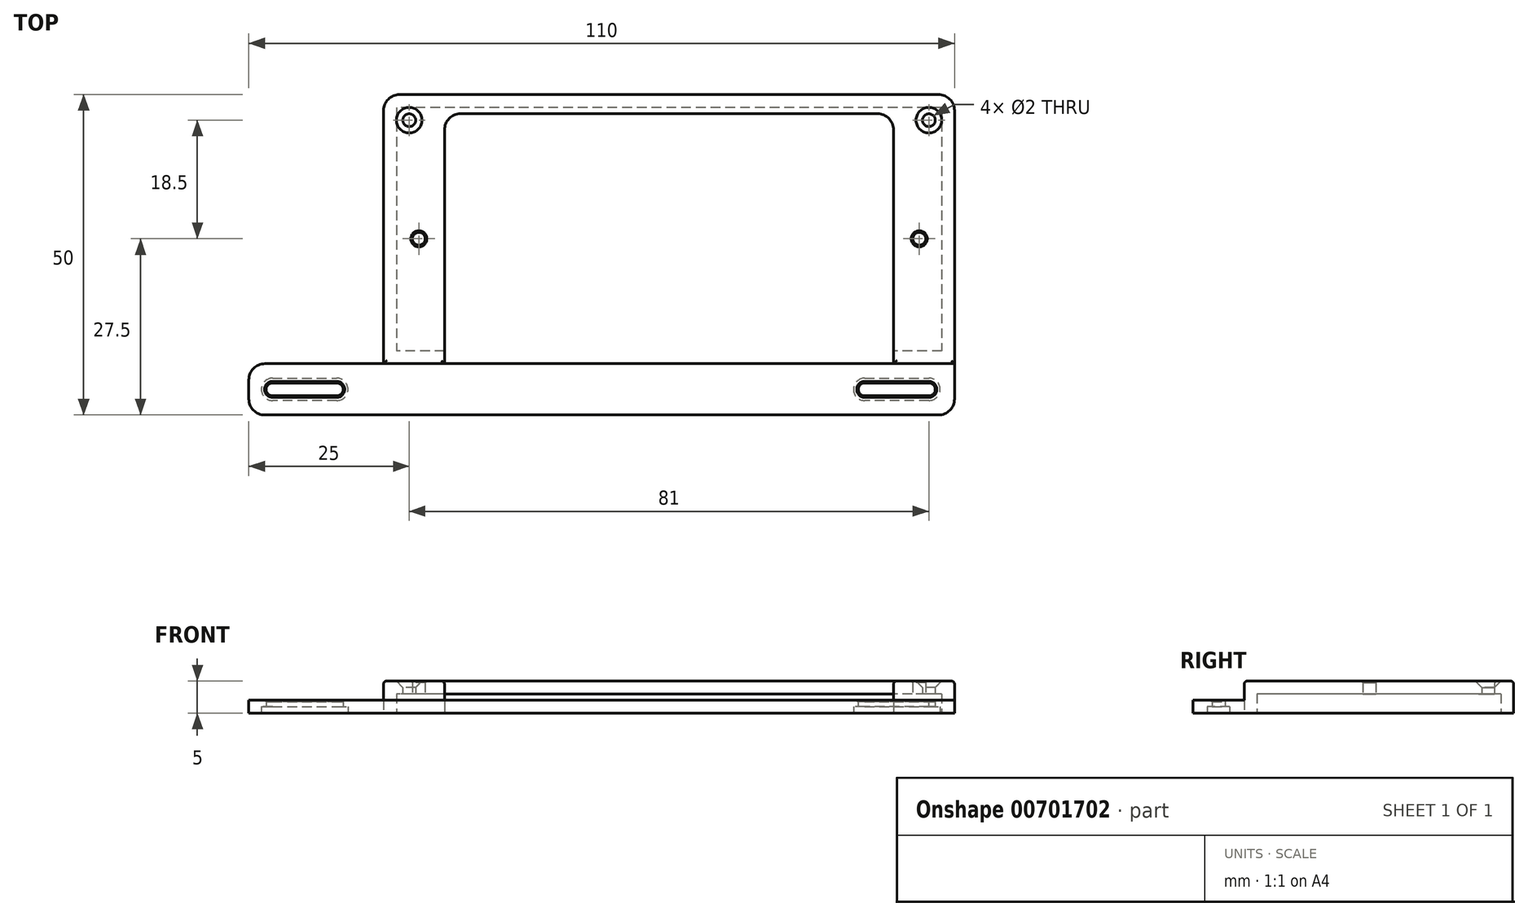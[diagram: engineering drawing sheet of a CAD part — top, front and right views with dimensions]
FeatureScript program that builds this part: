
annotation { "Feature Type Name" : "Feature", "Feature Type Description" : "" }
export const myFeature = defineFeature(function(context is Context, id is Id, definition is map)
    precondition{}
    {
        {
            var Q0;
            Q0=qCreatedBy(makeId("Top.planeOp"),FACE);
            var sketch = newSketch(context, id + "F0", { "sketchPlane" : qUnion([Q0])});
            skLineSegment(sketch, "E0.bottom", {"start": v(44.5, -22.5) * mm, "end": v(-44.5, -22.5) * mm});
            skLineSegment(sketch, "E0.top", {"start": v(44.5, 22.5) * mm, "end": v(-44.5, 22.5) * mm});
            skLineSegment(sketch, "E0.left", {"start": v(44.5, -22.5) * mm, "end": v(44.5, 22.5) * mm});
            skLineSegment(sketch, "E0.right", {"start": v(-44.5, -22.5) * mm, "end": v(-44.5, 22.5) * mm});
            skPoint(sketch, "E0.middle", {"position": v(0, 0) * mm});
            skSolve(sketch);
        }
        {
            var Q0;
            Q0=qCreatedBy(makeId("Top.planeOp"),FACE);
            var sketch = newSketch(context, id + "F1", { "sketchPlane" : qUnion([Q0])});
            skLineSegment(sketch, "E1.bottom", {"start": v(35, -19.5) * mm, "end": v(-35, -19.5) * mm});
            skLineSegment(sketch, "E1.top", {"start": v(35, 19.5) * mm, "end": v(-35, 19.5) * mm});
            skLineSegment(sketch, "E1.left", {"start": v(35, -19.5) * mm, "end": v(35, 19.5) * mm});
            skLineSegment(sketch, "E1.right", {"start": v(-35, -19.5) * mm, "end": v(-35, 19.5) * mm});
            skPoint(sketch, "E1.middle", {"position": v(0, 0) * mm});
            skSolve(sketch);
        }
        {
            var Q0;
            Q0=qCreatedBy(makeId("Top.planeOp"),FACE);
            var sketch = newSketch(context, id + "F2", { "sketchPlane" : qUnion([Q0])});
            skLineSegment(sketch, "E2.bottom", {"start": v(44.5, -19.5) * mm, "end": v(-65.5, -19.5) * mm});
            skLineSegment(sketch, "E2.top", {"start": v(44.5, -27.5) * mm, "end": v(-65.5, -27.5) * mm});
            skLineSegment(sketch, "E2.left", {"start": v(44.5, -19.5) * mm, "end": v(44.5, -27.5) * mm});
            skLineSegment(sketch, "E2.right", {"start": v(-65.5, -19.5) * mm, "end": v(-65.5, -27.5) * mm});
            skSolve(sketch);
        }
        {
            var Q0;
            Q0 = qSketchRegion(id + "F0", true);
            var Q1;
            Q1 = qSketchRegion(id + "F2", true);
            extrude(context, id + "F3", {"entities" : qUnion([Q0, Q1]), "depth" : 2 * mm, "offsetDistance" : 25 * mm});
        }
        {
            var Q0;
            Q0=qCreatedBy(makeId("Top.planeOp"),FACE);
            var sketch = newSketch(context, id + "F4", { "sketchPlane" : qUnion([Q0])});
            skLineSegment(sketch, "E3.bottom", {"start": v(-44.5, 22.5) * mm, "end": v(44.5, 22.5) * mm});
            skLineSegment(sketch, "E3.top", {"start": v(-44.5, -19.5) * mm, "end": v(44.5, -19.5) * mm});
            skLineSegment(sketch, "E3.left", {"start": v(-44.5, 22.5) * mm, "end": v(-44.5, -19.5) * mm});
            skLineSegment(sketch, "E3.right", {"start": v(44.5, 22.5) * mm, "end": v(44.5, -19.5) * mm});
            skSolve(sketch);
        }
        {
            var Q0;
            Q0 = qSketchRegion(id + "F4", true);
            extrude(context, id + "F5", {"entities" : qUnion([Q0]), "depth" : 5 * mm, "offsetDistance" : 25 * mm});
        }
        {
            var Q0;
            Q0=qCreatedBy(makeId("Top.planeOp"),FACE);
            var sketch = newSketch(context, id + "F6", { "sketchPlane" : qUnion([Q0])});
            skLineSegment(sketch, "E4.bottom", {"start": v(42.5, 20.5) * mm, "end": v(-42.5, 20.5) * mm});
            skLineSegment(sketch, "E4.top", {"start": v(42.5, -17.5) * mm, "end": v(-42.5, -17.5) * mm});
            skLineSegment(sketch, "E4.left", {"start": v(42.5, 20.5) * mm, "end": v(42.5, -17.5) * mm});
            skLineSegment(sketch, "E4.right", {"start": v(-42.5, 20.5) * mm, "end": v(-42.5, -17.5) * mm});
            skSolve(sketch);
        }
        {
            var Q0;
            Q0 = qSketchRegion(id + "F6", true);
            extrude(context, id + "F7", {"entities" : qUnion([Q0]), "operationType" : NewBodyOperationType.REMOVE, "depth" : 3 * mm, "offsetDistance" : 25 * mm});
        }
        {
            var Q0;
            Q0 = qSketchRegion(id + "F1", true);
            extrude(context, id + "F8", {"entities" : qUnion([Q0]), "operationType" : NewBodyOperationType.REMOVE, "depth" : 25 * mm, "offsetDistance" : 25 * mm});
        }
        {
            var Q0;
            Q0=makeQuery(id+"F3.opExtrude","SWEPT_BODY",BODY,{"disambiguationData":[OSD([sQuery(id+"F0.wireOp",EDGE,"E0.bottom"),sQuery(id+"F0.wireOp",EDGE,"E0.top"),sQuery(id+"F0.wireOp",EDGE,"E0.left"),sQuery(id+"F0.wireOp",EDGE,"E0.right")])]});
            var Q1;
            Q1=makeQuery(id+"F5.opExtrude","SWEPT_BODY",BODY,{"disambiguationData":[OSD([sQuery(id+"F4.wireOp",EDGE,"E3.bottom"),sQuery(id+"F4.wireOp",EDGE,"E3.top"),sQuery(id+"F4.wireOp",EDGE,"E3.left"),sQuery(id+"F4.wireOp",EDGE,"E3.right")])]});
            var Q2;
            Q2=makeQuery(id+"F3.opExtrude","SWEPT_BODY",BODY,{"disambiguationData":[OSD([sQuery(id+"F2.wireOp",EDGE,"E2.bottom"),sQuery(id+"F2.wireOp",EDGE,"E2.top"),sQuery(id+"F2.wireOp",EDGE,"E2.left"),sQuery(id+"F2.wireOp",EDGE,"E2.right")])]});
            booleanBodies(context, id + "F9", {"operationType" : BooleanOperationType.UNION, "tools" : qUnion([Q0, Q1, Q2])});
        }
        {
            var Q0;
            Q0=qCreatedBy(makeId("Top.planeOp"),FACE);
            var sketch = newSketch(context, id + "F10", { "sketchPlane" : qUnion([Q0])});
            skCircle(sketch, "E5", {"center": v(-40.5, 18.5) * mm, "radius": 1 * mm});
            skCircle(sketch, "E6", {"center": v(40.5, 18.5) * mm, "radius": 1 * mm});
            skSolve(sketch);
        }
        {
            var Q0;
            Q0=makeQuery(id+"F10.imprint","IMPRINT",FACE,{"disambiguationData":[TD([[makeQuery(id+"F10.imprint","IMPRINT",EDGE,{"derivedFrom":sQuery(id+"F10.wireOp",EDGE,"E5")}),1.0]])]});
            var Q1;
            Q1=makeQuery(id+"F10.imprint","IMPRINT",FACE,{"disambiguationData":[TD([[makeQuery(id+"F10.imprint","IMPRINT",EDGE,{"derivedFrom":sQuery(id+"F10.wireOp",EDGE,"E6")}),1.0]])]});
            extrude(context, id + "F11", {"entities" : qUnion([Q0, Q1]), "operationType" : NewBodyOperationType.REMOVE, "depth" : 25 * mm, "offsetDistance" : 25 * mm});
        }
        {
            var Q0;
            Q0=qCreatedBy(makeId("Top.planeOp"),FACE);
            var sketch = newSketch(context, id + "F12", { "sketchPlane" : qUnion([Q0])});
            skCircle(sketch, "E7", {"center": v(-39, 0) * mm, "radius": 1 * mm});
            skCircle(sketch, "E8", {"center": v(39, 0) * mm, "radius": 1 * mm});
            skSolve(sketch);
        }
        {
            var Q0;
            Q0 = qSketchRegion(id + "F12", true);
            extrude(context, id + "F13", {"entities" : qUnion([Q0]), "operationType" : NewBodyOperationType.REMOVE, "depth" : 25 * mm, "offsetDistance" : 25 * mm});
        }
        {
            var Q0;
            Q0=makeQuery(id+"F11.boolean.opBoolean","INTERSECT",EDGE,{"derivedFrom":[makeQuery(id+"F5.opExtrude","CAP_FACE",FACE,{"disambiguationData":[OSD([sQuery(id+"F4.wireOp",EDGE,"E3.bottom"),sQuery(id+"F4.wireOp",EDGE,"E3.top"),sQuery(id+"F4.wireOp",EDGE,"E3.left"),sQuery(id+"F4.wireOp",EDGE,"E3.right")])],"isStart":false}),makeQuery(id+"F11.opExtrude","SWEPT_FACE",FACE,{"disambiguationData":[OSD([sQuery(id+"F10.wireOp",EDGE,"E5")])]})]});
            var Q1;
            Q1=makeQuery(id+"F11.boolean.opBoolean","INTERSECT",EDGE,{"derivedFrom":[makeQuery(id+"F5.opExtrude","CAP_FACE",FACE,{"disambiguationData":[OSD([sQuery(id+"F4.wireOp",EDGE,"E3.bottom"),sQuery(id+"F4.wireOp",EDGE,"E3.top"),sQuery(id+"F4.wireOp",EDGE,"E3.left"),sQuery(id+"F4.wireOp",EDGE,"E3.right")])],"isStart":false}),makeQuery(id+"F11.opExtrude","SWEPT_FACE",FACE,{"disambiguationData":[OSD([sQuery(id+"F10.wireOp",EDGE,"E6")])]})]});
            chamfer(context, id + "F14", {"entities" : qUnion([Q0, Q1]), "chamferType" : ChamferType.OFFSET_ANGLE, "width" : 1 * mm, "oppositeDirection" : false, "angle" : 45 * degree, "tangentPropagation" : true});
        }
        {
            var Q0;
            Q0=makeQuery(id+"F9.opBoolean","MERGE",EDGE,{"derivedFrom":[makeQuery(id+"F3.opExtrude","SWEPT_EDGE",EDGE,{"disambiguationData":[OSD([sQuery(id+"F0.wireOp",EDGE,"E0.top"),sQuery(id+"F0.wireOp",EDGE,"E0.right")])]}),makeQuery(id+"F5.opExtrude","SWEPT_EDGE",EDGE,{"disambiguationData":[OSD([sQuery(id+"F4.wireOp",EDGE,"E3.bottom"),sQuery(id+"F4.wireOp",EDGE,"E3.left")])]})]});
            var Q1;
            Q1=makeQuery(id+"F9.opBoolean","MERGE",EDGE,{"derivedFrom":[makeQuery(id+"F3.opExtrude","SWEPT_EDGE",EDGE,{"disambiguationData":[OSD([sQuery(id+"F0.wireOp",EDGE,"E0.top"),sQuery(id+"F0.wireOp",EDGE,"E0.left")])]}),makeQuery(id+"F5.opExtrude","SWEPT_EDGE",EDGE,{"disambiguationData":[OSD([sQuery(id+"F4.wireOp",EDGE,"E3.bottom"),sQuery(id+"F4.wireOp",EDGE,"E3.right")])]})]});
            var Q2;
            Q2=makeQuery(id+"F3.opExtrude","SWEPT_EDGE",EDGE,{"disambiguationData":[OSD([sQuery(id+"F2.wireOp",EDGE,"E2.top"),sQuery(id+"F2.wireOp",EDGE,"E2.left")])]});
            var Q3;
            Q3=makeQuery(id+"F3.opExtrude","SWEPT_EDGE",EDGE,{"disambiguationData":[OSD([sQuery(id+"F2.wireOp",EDGE,"E2.top"),sQuery(id+"F2.wireOp",EDGE,"E2.right")])]});
            var Q4;
            Q4=makeQuery(id+"F3.opExtrude","SWEPT_EDGE",EDGE,{"disambiguationData":[OSD([sQuery(id+"F2.wireOp",EDGE,"E2.bottom"),sQuery(id+"F2.wireOp",EDGE,"E2.right")])]});
            var Q5;
            Q5=makeQuery(id+"F8.boolean.opBoolean","COPY",EDGE,{"derivedFrom":makeQuery(id+"F8.opExtrude","SWEPT_EDGE",EDGE,{"disambiguationData":[OSD([sQuery(id+"F1.wireOp",EDGE,"E1.top"),sQuery(id+"F1.wireOp",EDGE,"E1.right")])]})});
            var Q6;
            Q6=makeQuery(id+"F8.boolean.opBoolean","COPY",EDGE,{"derivedFrom":makeQuery(id+"F8.opExtrude","SWEPT_EDGE",EDGE,{"disambiguationData":[OSD([sQuery(id+"F1.wireOp",EDGE,"E1.top"),sQuery(id+"F1.wireOp",EDGE,"E1.left")])]})});
            fillet(context, id + "F15", {"entities" : qUnion([Q0, Q1, Q2, Q3, Q4, Q5, Q6]), "radius" : 2.5 * mm, "tangentPropagation" : true, "allowEdgeOverflow" : false});
        }
        {
            var Q0;
            {var subQ0=sQuery(id+"F4.wireOp",EDGE,"E3.left");var subQ1=sQuery(id+"F4.wireOp",EDGE,"E3.top");Q0=makeQuery(id+"F8.boolean.opBoolean","SPLIT",EDGE,{"disambiguationData":[TD([makeQuery(id+"F5.opExtrude","SWEPT_FACE",FACE,{"disambiguationData":[OSD([subQ0])]})])],"derivedFrom":makeQuery(id+"F5.opExtrude","CAP_EDGE",EDGE,{"disambiguationData":[OSD([subQ1])],"isStart":false})});}
            var Q1;
            Q1=makeQuery(id+"F5.opExtrude","CAP_EDGE",EDGE,{"disambiguationData":[OSD([sQuery(id+"F4.wireOp",EDGE,"E3.left")])],"isStart":false});
            var Q2;
            Q2=makeQuery(id+"F8.boolean.opBoolean","INTERSECT",EDGE,{"derivedFrom":[makeQuery(id+"F5.opExtrude","CAP_FACE",FACE,{"disambiguationData":[OSD([sQuery(id+"F4.wireOp",EDGE,"E3.bottom"),sQuery(id+"F4.wireOp",EDGE,"E3.top"),sQuery(id+"F4.wireOp",EDGE,"E3.left"),sQuery(id+"F4.wireOp",EDGE,"E3.right")])],"isStart":false}),makeQuery(id+"F8.opExtrude","SWEPT_FACE",FACE,{"disambiguationData":[OSD([sQuery(id+"F1.wireOp",EDGE,"E1.right")])]})]});
            var Q3;
            {var subQ0=sQuery(id+"F4.wireOp",EDGE,"E3.right");var subQ1=sQuery(id+"F4.wireOp",EDGE,"E3.top");Q3=makeQuery(id+"F8.boolean.opBoolean","SPLIT",EDGE,{"disambiguationData":[TD([makeQuery(id+"F5.opExtrude","SWEPT_FACE",FACE,{"disambiguationData":[OSD([subQ0])]})])],"derivedFrom":makeQuery(id+"F5.opExtrude","CAP_EDGE",EDGE,{"disambiguationData":[OSD([subQ1])],"isStart":false})});}
            fillet(context, id + "F16", {"entities" : qUnion([Q0, Q1, Q2, Q3]), "radius" : 0.5 * mm, "tangentPropagation" : true, "allowEdgeOverflow" : false});
        }
        {
            var Q0;
            Q0=qCreatedBy(makeId("Top.planeOp"),FACE);
            var sketch = newSketch(context, id + "F17", { "sketchPlane" : qUnion([Q0])});
            skLineSegment(sketch, "E9", {"start": v(42.5, -30.15) * mm, "end": v(-59.8, -30.15) * mm});
            skSolve(sketch);
        }
        {
            var Q0;
            Q0=qCreatedBy(makeId("Top.planeOp"),FACE);
            var sketch = newSketch(context, id + "F18", { "sketchPlane" : qUnion([Q0])});
            skCircle(sketch, "E10", {"center": v(-61.8, -23.5) * mm, "radius": 1 * mm});
            skCircle(sketch, "E11", {"center": v(40.5, -23.5) * mm, "radius": 1 * mm});
            skCircle(sketch, "E12.1.0.0", {"center": v(-51.8, -23.5) * mm, "radius": 1 * mm});
            skLineSegment(sketch, "E12.direction1", {"start": v(-61.8, -23.5) * mm, "end": v(-51.8, -23.5) * mm, "construction": true});
            skCircle(sketch, "E13.1.0.0", {"center": v(30.5, -23.5) * mm, "radius": 1 * mm});
            skLineSegment(sketch, "E13.direction1", {"start": v(40.5, -23.5) * mm, "end": v(30.5, -23.5) * mm, "construction": true});
            skLineSegment(sketch, "E14", {"start": v(-61.8, -22.5) * mm, "end": v(-51.8, -22.5) * mm});
            skLineSegment(sketch, "E15", {"start": v(-61.8, -24.5) * mm, "end": v(-51.8, -24.5) * mm});
            skLineSegment(sketch, "E16", {"start": v(30.5, -22.5) * mm, "end": v(40.5, -22.5) * mm});
            skLineSegment(sketch, "E17", {"start": v(40.52, -24.5) * mm, "end": v(30.5, -24.5) * mm});
            skSolve(sketch);
        }
        {
            var Q0;
            Q0 = qSketchRegion(id + "F18", true);
            extrude(context, id + "F19", {"entities" : qUnion([Q0]), "operationType" : NewBodyOperationType.REMOVE, "depth" : 25 * mm, "offsetDistance" : 25 * mm});
        }
        {
            var Q0;
            Q0=qCreatedBy(makeId("Top.planeOp"),FACE);
            var sketch = newSketch(context, id + "F20", { "sketchPlane" : qUnion([Q0])});
            skCircle(sketch, "E18", {"center": v(-61.8, -23.5) * mm, "radius": 1.75 * mm});
            skCircle(sketch, "E19", {"center": v(-51.8, -23.5) * mm, "radius": 1.75 * mm});
            skLineSegment(sketch, "E20", {"start": v(-61.8, -21.75) * mm, "end": v(-51.8, -21.75) * mm});
            skLineSegment(sketch, "E21", {"start": v(-51.8, -25.25) * mm, "end": v(-61.8, -25.25) * mm});
            skCircle(sketch, "E22", {"center": v(30.5, -23.5) * mm, "radius": 1.75 * mm});
            skCircle(sketch, "E23", {"center": v(40.5, -23.5) * mm, "radius": 1.75 * mm});
            skLineSegment(sketch, "E24", {"start": v(40.5, -25.25) * mm, "end": v(30.5, -25.25) * mm});
            skLineSegment(sketch, "E25", {"start": v(30.5, -21.75) * mm, "end": v(40.5, -21.75) * mm});
            skSolve(sketch);
        }
        {
            var Q0;
            Q0 = qSketchRegion(id + "F20", true);
            extrude(context, id + "F21", {"entities" : qUnion([Q0]), "operationType" : NewBodyOperationType.REMOVE, "depth" : 1 * mm, "offsetDistance" : 25 * mm});
        }
        {
            var Q0;
            Q0=makeQuery(id+"F19.boolean.opBoolean","INTERSECT",EDGE,{"derivedFrom":[makeQuery(id+"F9.opBoolean","MERGE",FACE,{"derivedFrom":[makeQuery(id+"F3.opExtrude","CAP_FACE",FACE,{"disambiguationData":[OSD([sQuery(id+"F2.wireOp",EDGE,"E2.bottom"),sQuery(id+"F2.wireOp",EDGE,"E2.top"),sQuery(id+"F2.wireOp",EDGE,"E2.left"),sQuery(id+"F2.wireOp",EDGE,"E2.right")])],"isStart":false}),makeQuery(id+"F3.opExtrude","CAP_FACE",FACE,{"disambiguationData":[OSD([sQuery(id+"F0.wireOp",EDGE,"E0.bottom"),sQuery(id+"F0.wireOp",EDGE,"E0.top"),sQuery(id+"F0.wireOp",EDGE,"E0.left"),sQuery(id+"F0.wireOp",EDGE,"E0.right")])],"isStart":false})]}),makeQuery(id+"F19.opExtrude","SWEPT_FACE",FACE,{"disambiguationData":[OSD([sQuery(id+"F18.wireOp",EDGE,"E14")])]})]});
            var Q1;
            Q1=makeQuery(id+"F19.boolean.opBoolean","INTERSECT",EDGE,{"derivedFrom":[makeQuery(id+"F9.opBoolean","MERGE",FACE,{"derivedFrom":[makeQuery(id+"F3.opExtrude","CAP_FACE",FACE,{"disambiguationData":[OSD([sQuery(id+"F2.wireOp",EDGE,"E2.bottom"),sQuery(id+"F2.wireOp",EDGE,"E2.top"),sQuery(id+"F2.wireOp",EDGE,"E2.left"),sQuery(id+"F2.wireOp",EDGE,"E2.right")])],"isStart":false}),makeQuery(id+"F3.opExtrude","CAP_FACE",FACE,{"disambiguationData":[OSD([sQuery(id+"F0.wireOp",EDGE,"E0.bottom"),sQuery(id+"F0.wireOp",EDGE,"E0.top"),sQuery(id+"F0.wireOp",EDGE,"E0.left"),sQuery(id+"F0.wireOp",EDGE,"E0.right")])],"isStart":false})]}),makeQuery(id+"F19.opExtrude","SWEPT_FACE",FACE,{"disambiguationData":[OSD([sQuery(id+"F18.wireOp",EDGE,"E16")])]})]});
            var Q2;
            Q2=makeQuery(id+"F13.boolean.opBoolean","INTERSECT",EDGE,{"derivedFrom":[makeQuery(id+"F5.opExtrude","CAP_FACE",FACE,{"disambiguationData":[OSD([sQuery(id+"F4.wireOp",EDGE,"E3.bottom"),sQuery(id+"F4.wireOp",EDGE,"E3.top"),sQuery(id+"F4.wireOp",EDGE,"E3.left"),sQuery(id+"F4.wireOp",EDGE,"E3.right")])],"isStart":false}),makeQuery(id+"F13.opExtrude","SWEPT_FACE",FACE,{"disambiguationData":[OSD([sQuery(id+"F12.wireOp",EDGE,"E7")])]})]});
            var Q3;
            Q3=makeQuery(id+"F13.boolean.opBoolean","INTERSECT",EDGE,{"derivedFrom":[makeQuery(id+"F5.opExtrude","CAP_FACE",FACE,{"disambiguationData":[OSD([sQuery(id+"F4.wireOp",EDGE,"E3.bottom"),sQuery(id+"F4.wireOp",EDGE,"E3.top"),sQuery(id+"F4.wireOp",EDGE,"E3.left"),sQuery(id+"F4.wireOp",EDGE,"E3.right")])],"isStart":false}),makeQuery(id+"F13.opExtrude","SWEPT_FACE",FACE,{"disambiguationData":[OSD([sQuery(id+"F12.wireOp",EDGE,"E8")])]})]});
            chamfer(context, id + "F22", {"entities" : qUnion([Q0, Q1, Q2, Q3]), "width" : 0.25 * mm, "tangentPropagation" : true});
        }
    });
